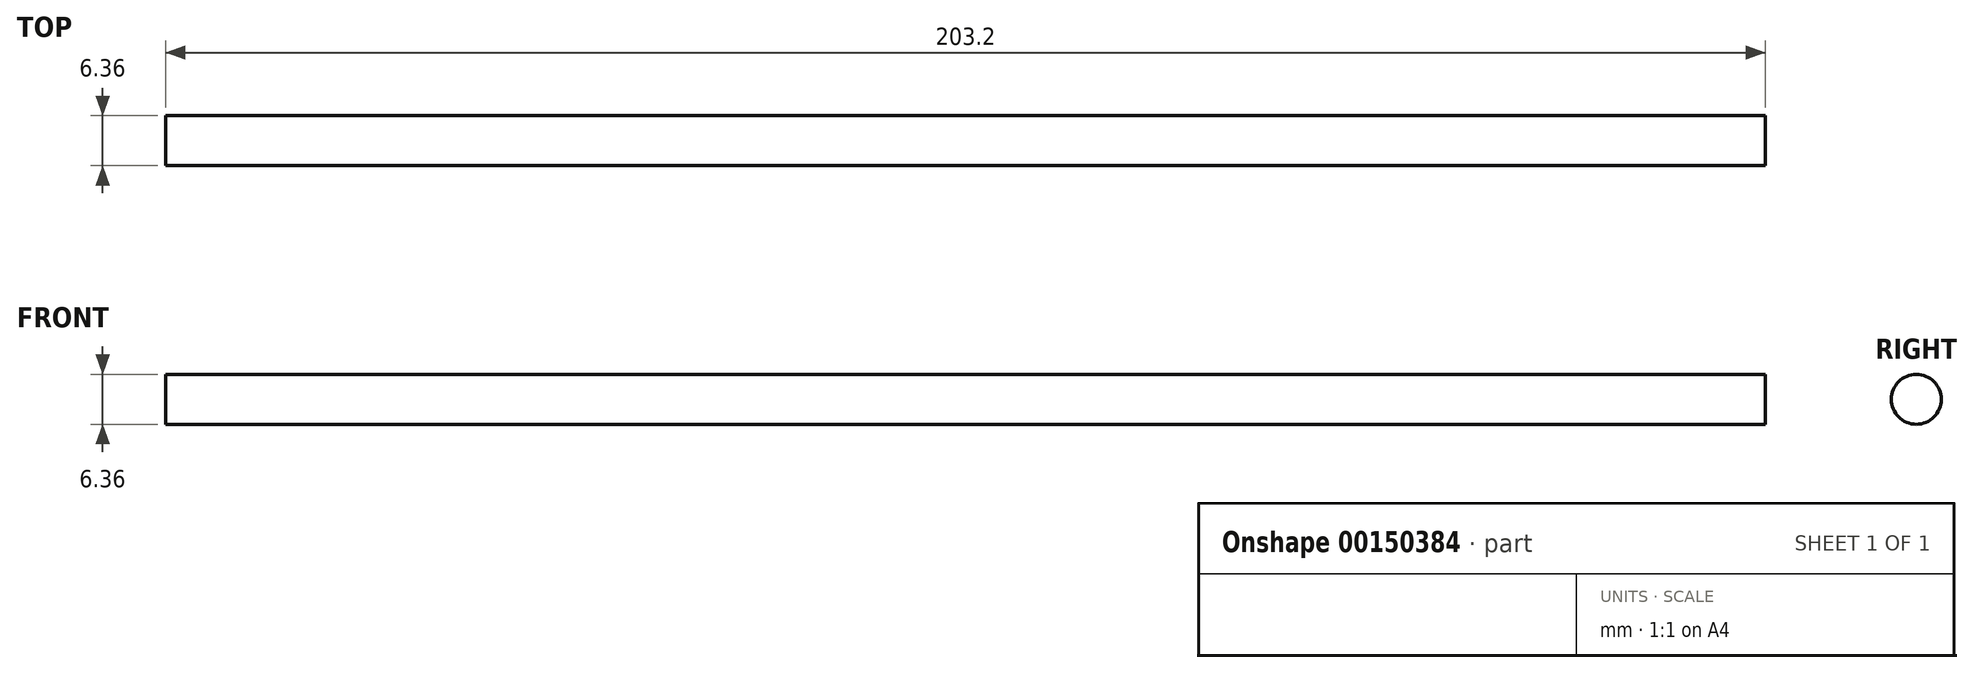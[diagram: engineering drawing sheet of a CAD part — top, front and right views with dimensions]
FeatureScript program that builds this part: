
annotation { "Feature Type Name" : "Feature", "Feature Type Description" : "" }
export const myFeature = defineFeature(function(context is Context, id is Id, definition is map)
    precondition{}
    {
        {
            var Q0;
            Q0=qCreatedBy(makeId("Right.planeOp"),FACE);
            var sketch = newSketch(context, id + "F0", { "sketchPlane" : qUnion([Q0])});
            skCircle(sketch, "E0", {"center": v(0, 0) * mm, "radius": 3.18 * mm});
            skSolve(sketch);
        }
        {
            var Q0;
            Q0 = qSketchRegion(id + "F0", true);
            extrude(context, id + "F1", {"entities" : qUnion([Q0]), "depth" : 203.2 * mm});
        }
    });
